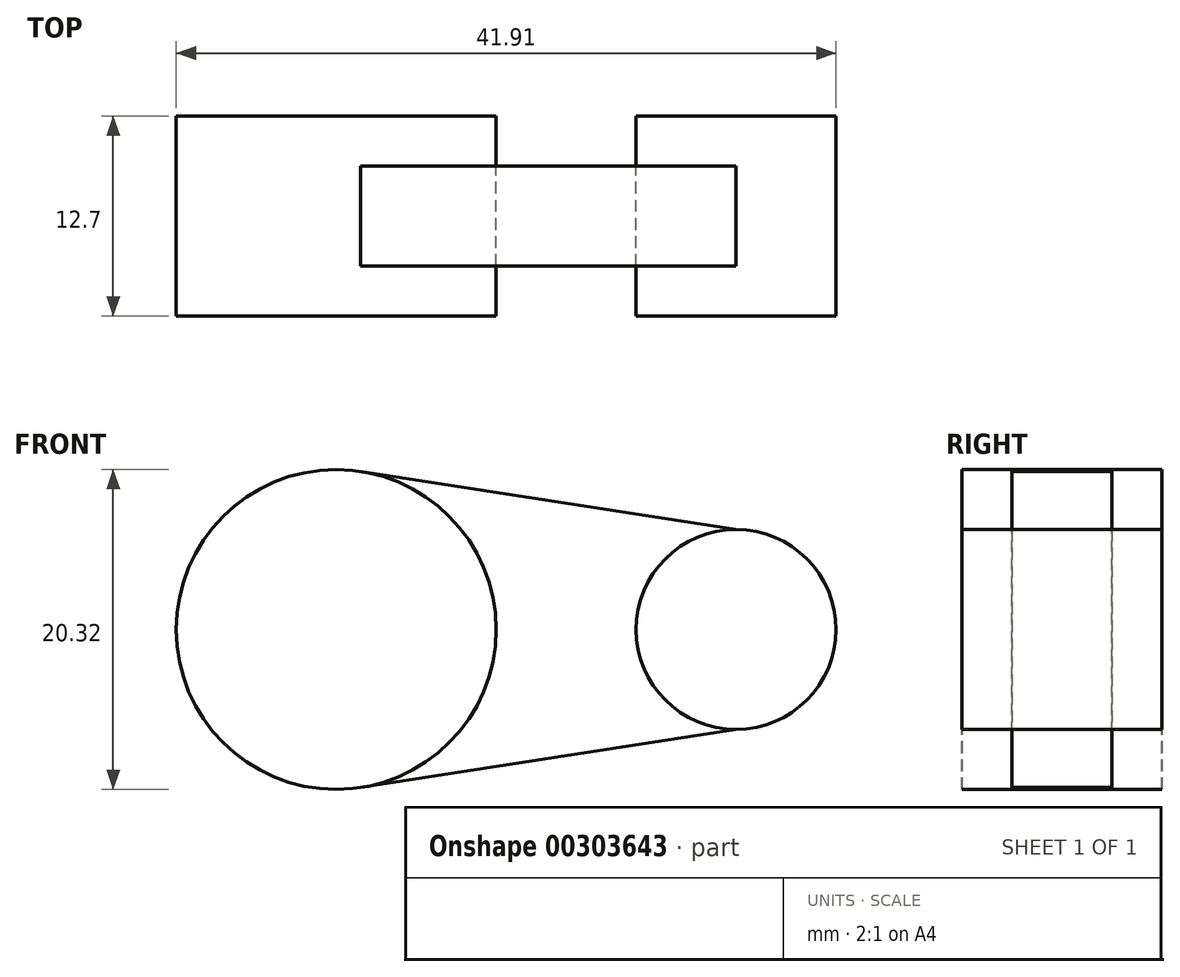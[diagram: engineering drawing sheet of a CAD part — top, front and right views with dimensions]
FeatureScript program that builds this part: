
annotation { "Feature Type Name" : "Feature", "Feature Type Description" : "" }
export const myFeature = defineFeature(function(context is Context, id is Id, definition is map)
    precondition{}
    {
        {
            var Q0;
            Q0=qCreatedBy(makeId("Front.planeOp"),FACE);
            var sketch = newSketch(context, id + "F0", { "sketchPlane" : qUnion([Q0])});
            skLineSegment(sketch, "E0", {"start": v(0, 0) * mm, "end": v(25.4, 0) * mm});
            skCircle(sketch, "E1", {"center": v(0, 0) * mm, "radius": 10.16 * mm});
            skCircle(sketch, "E2", {"center": v(25.4, 0) * mm, "radius": 6.35 * mm});
            skLineSegment(sketch, "E3", {"start": v(25.4, 6.35) * mm, "end": v(0, 10.28) * mm});
            skLineSegment(sketch, "E4.MirrorCS", {"start": v(25.4, -6.35) * mm, "end": v(0, -10.28) * mm});
            skSolve(sketch);
        }
        {
            var Q0;
            {var subQ0=sQuery(id+"F0.wireOp",EDGE,"E1");var subQ1=makeQuery(id+"F0.imprint","INTERSECT",VERTEX,{"derivedFrom":[subQ0,sQuery(id+"F0.wireOp",EDGE,"E3")]});Q0=makeQuery(id+"F0.imprint","IMPRINT",FACE,{"disambiguationData":[TD([[makeQuery(id+"F0.imprint","IMPRINT",EDGE,{"disambiguationData":[TD([[subQ1,1.0]])],"derivedFrom":subQ0}),1.0]])]});}
            extrude(context, id + "F1", {"entities" : qUnion([Q0]), "endBound" : BoundingType.SYMMETRIC, "depth" : 12.7 * mm});
        }
        {
            var Q0;
            {var subQ0=sQuery(id+"F0.wireOp",EDGE,"E2");var subQ1=makeQuery(id+"F0.imprint","INTERSECT",VERTEX,{"derivedFrom":[subQ0,sQuery(id+"F0.wireOp",EDGE,"E3")]});Q0=makeQuery(id+"F0.imprint","IMPRINT",FACE,{"disambiguationData":[TD([[makeQuery(id+"F0.imprint","IMPRINT",EDGE,{"disambiguationData":[TD([[subQ1,-1.0]])],"derivedFrom":subQ0}),1.0]])]});}
            extrude(context, id + "F2", {"entities" : qUnion([Q0]), "endBound" : BoundingType.SYMMETRIC, "depth" : 12.7 * mm});
        }
        {
            var Q0;
            {var subQ0=sQuery(id+"F0.wireOp",EDGE,"E1");var subQ1=sQuery(id+"F0.wireOp",EDGE,"E0");var subQ2=makeQuery(id+"F0.imprint","INTERSECT",VERTEX,{"derivedFrom":[subQ1,subQ0]});Q0=makeQuery(id+"F0.imprint","IMPRINT",FACE,{"disambiguationData":[TD([[makeQuery(id+"F0.imprint","IMPRINT",EDGE,{"disambiguationData":[TD([[subQ2,-1.0]])],"derivedFrom":subQ1}),1.0]])]});}
            var Q1;
            {var subQ0=sQuery(id+"F0.wireOp",EDGE,"E1");var subQ1=sQuery(id+"F0.wireOp",EDGE,"E0");var subQ2=makeQuery(id+"F0.imprint","INTERSECT",VERTEX,{"derivedFrom":[subQ1,subQ0]});Q1=makeQuery(id+"F0.imprint","IMPRINT",FACE,{"disambiguationData":[TD([[makeQuery(id+"F0.imprint","IMPRINT",EDGE,{"disambiguationData":[TD([[subQ2,-1.0]])],"derivedFrom":subQ1}),-1.0]])]});}
            extrude(context, id + "F3", {"entities" : qUnion([Q0, Q1]), "endBound" : BoundingType.SYMMETRIC, "depth" : 6.35 * mm});
        }
    });
